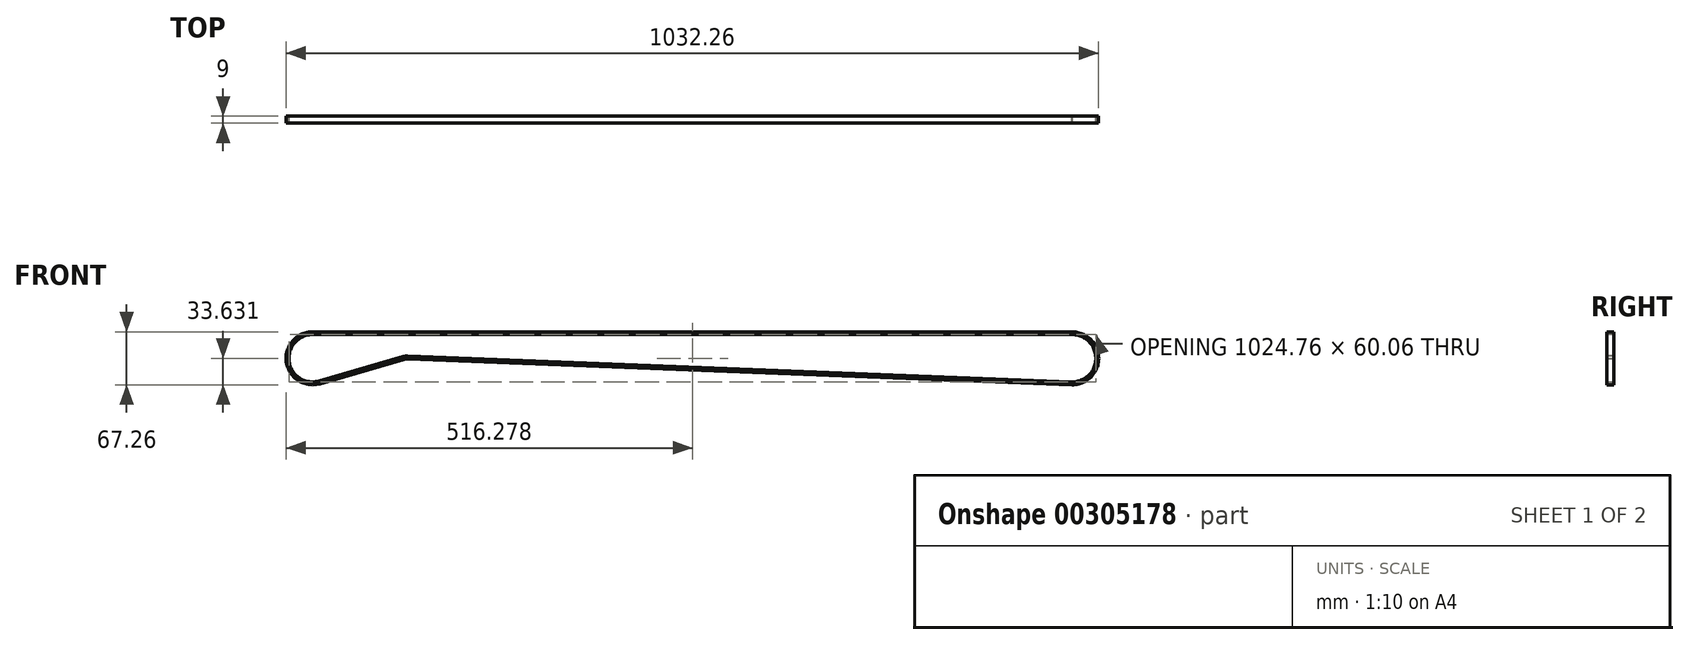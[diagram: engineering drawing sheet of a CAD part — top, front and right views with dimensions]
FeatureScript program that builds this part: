
annotation { "Feature Type Name" : "Feature", "Feature Type Description" : "" }
export const myFeature = defineFeature(function(context is Context, id is Id, definition is map)
    precondition{}
    {
        {
            var Q0;
            Q0=qCreatedBy(makeId("Front.planeOp"),FACE);
            var sketch = newSketch(context, id + "F0", { "sketchPlane" : qUnion([Q0])});
            skLineSegment(sketch, "E0", {"start": v(96.05, -68.86) * mm, "end": v(96.05, -68.86) * mm});
            skLineSegment(sketch, "E1", {"start": v(-472.24, -585.2) * mm, "end": v(492.76, -585.2) * mm, "construction": true});
            skPoint(sketch, "E2.centerSnap0", {"position": v(10.26, -585.2) * mm});
            skLineSegment(sketch, "E3", {"start": v(-472.24, -553.38) * mm, "end": v(492.76, -553.38) * mm});
            skCircle(sketch, "E4", {"center": v(705.76, -585.2) * mm, "radius": 31.83 * mm});
            skLineSegment(sketch, "E5", {"start": v(492.36, -617.04) * mm, "end": v(-351.62, -584.22) * mm});
            skLineSegment(sketch, "E6", {"start": v(-463.38, -615.78) * mm, "end": v(-356.7, -584.84) * mm});
            skArc(sketch, "E7", {"start": v(-356.7, -584.84) * mm, "mid": v(-350.3, -616.1) * mm, "end": v(-351.62, -584.22) * mm});
            skArc(sketch, "E8", {"start": v(-351.62, -584.22) * mm, "mid": v(-354.18, -584.33) * mm, "end": v(-356.7, -584.84) * mm});
            skArc(sketch, "E9", {"start": v(-463.38, -615.78) * mm, "mid": v(-440.73, -580.73) * mm, "end": v(-472.24, -553.38) * mm});
            skArc(sketch, "E10", {"start": v(-472.24, -553.38) * mm, "mid": v(-503.75, -589.69) * mm, "end": v(-463.38, -615.78) * mm});
            skArc(sketch, "E11", {"start": v(492.36, -617.04) * mm, "mid": v(524.59, -585.4) * mm, "end": v(492.76, -553.38) * mm});
            skArc(sketch, "E12", {"start": v(492.76, -553.38) * mm, "mid": v(460.93, -585.01) * mm, "end": v(492.36, -617.04) * mm});
            skSolve(sketch);
        }
        {
            var Q0;
            Q0=sQuery(id+"F0.wireOp",EDGE,"E3");
            cPlane(context, id + "F1", {"entities" : qUnion([Q0]), "cplaneType" : CPlaneType.MID_PLANE, "offset" : 25 * mm, "width" : 150 * mm, "height" : 150 * mm});
        }
        {
            var Q0;
            Q0=qCreatedBy(id+"F1.planeOp",FACE);
            var sketch = newSketch(context, id + "F2", { "sketchPlane" : qUnion([Q0])});
            skPoint(sketch, "E13.0", {"position": v(0, -553.38) * mm});
            skLineSegment(sketch, "E14.bottom", {"start": v(4.5, -551.58) * mm, "end": v(-4.5, -551.58) * mm});
            skLineSegment(sketch, "E14.top", {"start": v(4.5, -555.18) * mm, "end": v(-4.5, -555.18) * mm});
            skLineSegment(sketch, "E14.left", {"start": v(4.5, -551.58) * mm, "end": v(4.5, -555.18) * mm});
            skLineSegment(sketch, "E14.right", {"start": v(-4.5, -551.58) * mm, "end": v(-4.5, -555.18) * mm});
            skSolve(sketch);
        }
        {
            var Q0;
            Q0=makeQuery(id+"F2.imprint","IMPRINT",FACE,{"disambiguationData":[TD([[makeQuery(id+"F2.imprint","IMPRINT",EDGE,{"derivedFrom":sQuery(id+"F2.wireOp",EDGE,"E14.bottom")}),1.0]])]});
            var Q1;
            Q1=sQuery(id+"F0.wireOp",EDGE,"E3");
            var Q2;
            Q2=sQuery(id+"F0.wireOp",EDGE,"E10");
            var Q3;
            Q3=sQuery(id+"F0.wireOp",EDGE,"E6");
            var Q4;
            Q4=sQuery(id+"F0.wireOp",EDGE,"E8");
            var Q5;
            Q5=sQuery(id+"F0.wireOp",EDGE,"E5");
            var Q6;
            Q6=sQuery(id+"F0.wireOp",EDGE,"E11");
            sweep(context, id + "F3", {"profiles" : qUnion([Q0]), "path" : qUnion([Q1, Q2, Q3, Q4, Q5, Q6])});
        }
    });
